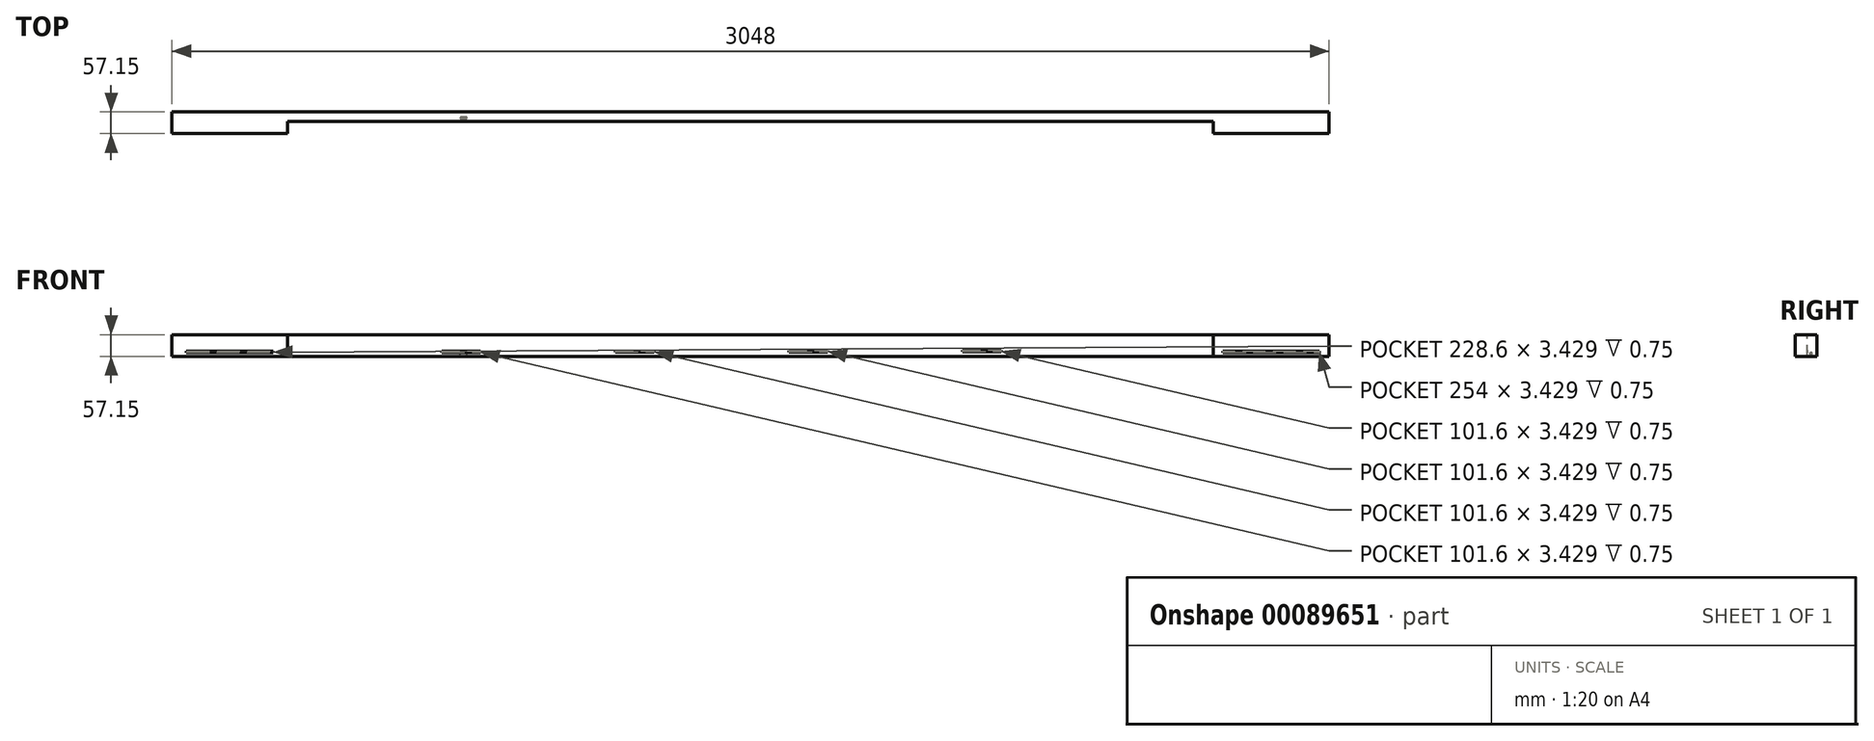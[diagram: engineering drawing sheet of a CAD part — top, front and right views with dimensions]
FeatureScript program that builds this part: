
annotation { "Feature Type Name" : "Feature", "Feature Type Description" : "" }
export const myFeature = defineFeature(function(context is Context, id is Id, definition is map)
    precondition{}
    {
        {
            var Q0;
            Q0=qCreatedBy(makeId("Top.planeOp"),FACE);
            var sketch = newSketch(context, id + "F0", { "sketchPlane" : qUnion([Q0])});
            skLineSegment(sketch, "E0.bottom", {"start": v(-1528.86, -333.75) * mm, "end": v(1519.14, -333.75) * mm});
            skLineSegment(sketch, "E0.top", {"start": v(-1528.86, -276.6) * mm, "end": v(1519.14, -276.6) * mm});
            skLineSegment(sketch, "E0.left", {"start": v(-1528.86, -333.75) * mm, "end": v(-1528.86, -276.6) * mm});
            skLineSegment(sketch, "E0.right", {"start": v(1519.14, -333.75) * mm, "end": v(1519.14, -276.6) * mm});
            skSolve(sketch);
        }
        {
            assignVariable(context, id + "F1", {"name" : "y", "anyValue" : .75});
        }
        {
            var Q0;
            Q0 = qSketchRegion(id + "F0", true);
            extrude(context, id + "F2", {"entities" : qUnion([Q0]), "depth" : 57.15 * mm});
        }
        {
            var Q0;
            Q0=makeQuery(id+"F2.opExtrude","CAP_FACE",FACE,{"disambiguationData":[OSD([sQuery(id+"F0.wireOp",EDGE,"E0.bottom"),sQuery(id+"F0.wireOp",EDGE,"E0.top"),sQuery(id+"F0.wireOp",EDGE,"E0.left"),sQuery(id+"F0.wireOp",EDGE,"E0.right")])],"isStart":false});
            var sketch = newSketch(context, id + "F3", { "sketchPlane" : qUnion([Q0])});
            skLineSegment(sketch, "E1.bottom", {"start": v(-1224.06, -333.75) * mm, "end": v(1214.34, -333.75) * mm});
            skLineSegment(sketch, "E1.top", {"start": v(-1224.06, -302) * mm, "end": v(1214.34, -302) * mm});
            skLineSegment(sketch, "E1.left", {"start": v(-1224.06, -333.75) * mm, "end": v(-1224.06, -302) * mm});
            skLineSegment(sketch, "E1.right", {"start": v(1214.34, -333.75) * mm, "end": v(1214.34, -302) * mm});
            skSolve(sketch);
        }
        {
            var Q0;
            Q0 = qSketchRegion(id + "F3", true);
            extrude(context, id + "F4", {"entities" : qUnion([Q0]), "operationType" : NewBodyOperationType.REMOVE, "endBound" : BoundingType.UP_TO_NEXT, "oppositeDirection" : true, "depth" : 25.4 * mm});
        }
        {
            var Q0;
            {var subQ1=sQuery(id+"F0.wireOp",EDGE,"E0.left");var subQ3=sQuery(id+"F0.wireOp",EDGE,"E0.bottom");Q0=makeQuery(id+"F4.boolean.opBoolean","SPLIT",FACE,{"disambiguationData":[TD([makeQuery(id+"F2.opExtrude","SWEPT_FACE",FACE,{"disambiguationData":[OSD([subQ1])]})])],"derivedFrom":makeQuery(id+"F2.opExtrude","SWEPT_FACE",FACE,{"disambiguationData":[OSD([subQ3])]})});}
            var sketch = newSketch(context, id + "F5", { "sketchPlane" : qUnion([Q0])});
            skLineSegment(sketch, "E2.bottom", {"start": v(-1490.76, 9.53) * mm, "end": v(-1262.16, 9.53) * mm});
            skLineSegment(sketch, "E2.top", {"start": v(-1490.76, 12.95) * mm, "end": v(-1262.16, 12.95) * mm});
            skLineSegment(sketch, "E2.left", {"start": v(-1490.76, 9.53) * mm, "end": v(-1490.76, 12.95) * mm});
            skLineSegment(sketch, "E2.right", {"start": v(-1262.16, 9.52) * mm, "end": v(-1262.16, 12.95) * mm});
            skSolve(sketch);
        }
        {
            var Q0;
            Q0=makeQuery(id+"F5.imprint","IMPRINT",FACE,{"disambiguationData":[TD([[makeQuery(id+"F5.imprint","IMPRINT",EDGE,{"derivedFrom":sQuery(id+"F5.wireOp",EDGE,"E2.bottom")}),1.0]])]});
            extrude(context, id + "F6", {"entities" : qUnion([Q0]), "operationType" : NewBodyOperationType.REMOVE, "oppositeDirection" : true, "depth" : (getVariable(context, 'y')) * mm});
        }
        {
            var Q0;
            {var subQ0=sQuery(id+"F0.wireOp",EDGE,"E0.right");var subQ3=sQuery(id+"F0.wireOp",EDGE,"E0.bottom");Q0=makeQuery(id+"F4.boolean.opBoolean","SPLIT",FACE,{"disambiguationData":[TD([makeQuery(id+"F2.opExtrude","SWEPT_FACE",FACE,{"disambiguationData":[OSD([subQ0])]})])],"derivedFrom":makeQuery(id+"F2.opExtrude","SWEPT_FACE",FACE,{"disambiguationData":[OSD([subQ3])]})});}
            var sketch = newSketch(context, id + "F7", { "sketchPlane" : qUnion([Q0])});
            skLineSegment(sketch, "E3.bottom", {"start": v(1239.74, 9.53) * mm, "end": v(1493.74, 9.53) * mm});
            skLineSegment(sketch, "E3.top", {"start": v(1239.74, 12.95) * mm, "end": v(1493.74, 12.95) * mm});
            skLineSegment(sketch, "E3.left", {"start": v(1239.74, 9.53) * mm, "end": v(1239.74, 12.95) * mm});
            skLineSegment(sketch, "E3.right", {"start": v(1493.74, 9.52) * mm, "end": v(1493.74, 12.95) * mm});
            skSolve(sketch);
        }
        {
            var Q0;
            Q0=makeQuery(id+"F7.imprint","IMPRINT",FACE,{"disambiguationData":[TD([[makeQuery(id+"F7.imprint","IMPRINT",EDGE,{"derivedFrom":sQuery(id+"F7.wireOp",EDGE,"E3.bottom")}),1.0]])]});
            extrude(context, id + "F8", {"entities" : qUnion([Q0]), "operationType" : NewBodyOperationType.REMOVE, "oppositeDirection" : true, "depth" : (getVariable(context, 'y')) * mm});
        }
        {
            var Q0;
            Q0=makeQuery(id+"F4.boolean.opBoolean","COPY",FACE,{"derivedFrom":makeQuery(id+"F4.opExtrude","SWEPT_FACE",FACE,{"disambiguationData":[OSD([sQuery(id+"F3.wireOp",EDGE,"E1.top")])]})});
            var sketch = newSketch(context, id + "F9", { "sketchPlane" : qUnion([Q0])});
            skLineSegment(sketch, "E4.bottom", {"start": v(-817.66, 9.53) * mm, "end": v(-716.06, 9.53) * mm});
            skLineSegment(sketch, "E4.top", {"start": v(-817.66, 12.95) * mm, "end": v(-716.06, 12.95) * mm});
            skLineSegment(sketch, "E4.left", {"start": v(-817.66, 9.53) * mm, "end": v(-817.66, 12.95) * mm});
            skLineSegment(sketch, "E4.right", {"start": v(-716.06, 9.53) * mm, "end": v(-716.06, 12.95) * mm});
            skLineSegment(sketch, "E5.1.0.0", {"start": v(-360.46, 10.42) * mm, "end": v(-258.86, 10.42) * mm});
            skLineSegment(sketch, "E5.1.0.1", {"start": v(-360.46, 13.85) * mm, "end": v(-258.86, 13.85) * mm});
            skLineSegment(sketch, "E5.1.0.2", {"start": v(-360.46, 10.42) * mm, "end": v(-360.46, 13.85) * mm});
            skLineSegment(sketch, "E5.1.0.3", {"start": v(-258.86, 10.42) * mm, "end": v(-258.86, 13.85) * mm});
            skLineSegment(sketch, "E5.2.0.0", {"start": v(96.74, 11.32) * mm, "end": v(198.34, 11.32) * mm});
            skLineSegment(sketch, "E5.2.0.1", {"start": v(96.74, 14.74) * mm, "end": v(198.34, 14.74) * mm});
            skLineSegment(sketch, "E5.2.0.2", {"start": v(96.74, 11.32) * mm, "end": v(96.74, 14.74) * mm});
            skLineSegment(sketch, "E5.2.0.3", {"start": v(198.34, 11.32) * mm, "end": v(198.34, 14.74) * mm});
            skLineSegment(sketch, "E5.3.0.0", {"start": v(553.94, 12.21) * mm, "end": v(655.54, 12.21) * mm});
            skLineSegment(sketch, "E5.3.0.1", {"start": v(553.94, 15.64) * mm, "end": v(655.54, 15.64) * mm});
            skLineSegment(sketch, "E5.3.0.2", {"start": v(553.94, 12.21) * mm, "end": v(553.94, 15.64) * mm});
            skLineSegment(sketch, "E5.3.0.3", {"start": v(655.54, 12.21) * mm, "end": v(655.54, 15.64) * mm});
            skLineSegment(sketch, "E5.direction1", {"start": v(-817.66, 9.53) * mm, "end": v(-360.46, 10.42) * mm, "construction": true});
            skPoint(sketch, "E6", {"position": v(-766.86, 9.53) * mm});
            skSolve(sketch);
        }
        {
            var Q0;
            Q0=makeQuery(id+"F9.imprint","IMPRINT",FACE,{"disambiguationData":[TD([[makeQuery(id+"F9.imprint","IMPRINT",EDGE,{"derivedFrom":sQuery(id+"F9.wireOp",EDGE,"E4.bottom")}),1.0]])]});
            var Q1;
            Q1=makeQuery(id+"F9.imprint","IMPRINT",FACE,{"disambiguationData":[TD([[makeQuery(id+"F9.imprint","IMPRINT",EDGE,{"derivedFrom":sQuery(id+"F9.wireOp",EDGE,"E5.1.0.0")}),1.0]])]});
            var Q2;
            Q2=makeQuery(id+"F9.imprint","IMPRINT",FACE,{"disambiguationData":[TD([[makeQuery(id+"F9.imprint","IMPRINT",EDGE,{"derivedFrom":sQuery(id+"F9.wireOp",EDGE,"E5.2.0.0")}),1.0]])]});
            var Q3;
            Q3=makeQuery(id+"F9.imprint","IMPRINT",FACE,{"disambiguationData":[TD([[makeQuery(id+"F9.imprint","IMPRINT",EDGE,{"derivedFrom":sQuery(id+"F9.wireOp",EDGE,"E5.3.0.0")}),1.0]])]});
            extrude(context, id + "F10", {"entities" : qUnion([Q0, Q1, Q2, Q3]), "operationType" : NewBodyOperationType.REMOVE, "oppositeDirection" : true, "depth" : (getVariable(context, 'y')) * mm});
        }
        {
            var Q0;
            Q0=makeQuery(id+"F10.boolean.opBoolean","COPY",FACE,{"derivedFrom":makeQuery(id+"F10.opExtrude","SWEPT_FACE",FACE,{"disambiguationData":[OSD([sQuery(id+"F9.wireOp",EDGE,"E4.bottom")])]})});
            var sketch = newSketch(context, id + "F11", { "sketchPlane" : qUnion([Q0])});
            skArc(sketch, "E7", {"start": v(-766.86, -289.93) * mm, "mid": v(-769.4, -292.47) * mm, "end": v(-766.86, -295.01) * mm});
            skPoint(sketch, "E7.centerSnap0", {"position": v(-766.86, -282.95) * mm});
            skPoint(sketch, "E7.centerSnap1", {"position": v(-817.66, -292.47) * mm});
            skArc(sketch, "E8", {"start": v(-754.16, -295.01) * mm, "mid": v(-751.62, -292.47) * mm, "end": v(-754.16, -289.93) * mm});
            skLineSegment(sketch, "E9.bottom", {"start": v(-766.86, -295.01) * mm, "end": v(-754.16, -295.01) * mm});
            skLineSegment(sketch, "E9.top", {"start": v(-766.86, -289.93) * mm, "end": v(-754.16, -289.93) * mm});
            skSolve(sketch);
        }
        {
            var Q0;
            Q0=makeQuery(id+"F11.imprint","IMPRINT",FACE,{"disambiguationData":[TD([[makeQuery(id+"F11.imprint","IMPRINT",EDGE,{"derivedFrom":sQuery(id+"F11.wireOp",EDGE,"E7")}),1.0]])]});
            extrude(context, id + "F12", {"entities" : qUnion([Q0]), "operationType" : NewBodyOperationType.REMOVE, "endBound" : BoundingType.UP_TO_NEXT, "oppositeDirection" : true, "depth" : 25.4 * mm});
        }
    });
